# Revit family: LR1685-W-2
name_source: partatom
category: Plumbing Fixtures
revit_build: Autodesk Revit MEP 2016 (Build: 20150220_1215(x64)
units: mm (PartAtom-declared; Revit-internal decimal feet)

## family parameters
Cut with Voids When Loaded = No
Host = Face
OmniClass Number = 23.45.05.21.11.11
OmniClass Title = Water Operated Water Closets
Part Type = Normal
Room Calculation Point = No
Round Connector Dimension = Use Diameter
Shared = Yes

## types (1)
- LR1685-W-2
    2- On-Floor, Wall Outlet = Yes
    ADA - 18" Integral Seat Height = No
    CO1 - Cleanout w/ O-Ring Connection to No-Hub 4" (Plain End Only) = No
    CO1-3 - Cleanout w/ O-Ring Connection to No-Hub 3" (Plain End Only) = No
    COH - Cleanout Hook Assembly = No
    CW Connection = No
    Default Elevation = 15"
    Description = Ligature Resistant Blowout Jet Toilet Bowl -On Floor-
    EG - Enviro-Glaze Toilet Exterior & Interior Color Specify = No
    EGE -EG - Enviro-Glaze Toilet Exterior Only Color Specify = No
    EVSFV- Master-Trol Electronic Flush Valve (N/A for Top Supply) = No
    EVSPFV- Master-Trol Electronic Flush Valve w/ Piezo Button (N/A for Top Supply) = No
    FT - Flood-Trol (N/A With Top Supply) = No
    FTA - Flood-Trol Auto-Reset (N/A with Top Supply) = No
    FTE - Flood-Trol Electronic = No
    FV- Flush Valve, Mechanical (N/A for ADA) = 0"
    FVBO- Flush Valve by Others = No
    FVH- Flush Valve, Hydraulic (N/A for Top Supply) = No
    FVT - Flush Thru-Wall Connector = No
    GW - Gasketed Toilet Waste = No
    HET- 1.28 GPF = No
    HPS - High Polish Integral Seat = No
    HW Connection = No
    LR1685- Ligature Resistant Blowout Jet Toilet = Yes
    MT - Metal Template (Only 1 Repuired Per Project) = No
    MTPFV- Master-Trol Plus Electronic Flush Valve (N/A for Top Supply) = No
    MTPPFV- Master-Trol Plus Electronic Flush Valve W/ Piezo Button (N/A for Top Supply) = No
    MVCFV- Time-Trol Plus Electronic Flush Valve (N/A for Top Supply) = No
    Manufacturer = Acorn Engineering
    Material = Type 304 Stainless Steel
    Model = LR1685-W-2
    PC - Pinned Cleanout Plug (For -C01 Options Above) = No
    SW - Wall Sleeve = No
    T- Top (exposed) = No
    TF - Transformer 120VAC to 24 VAC (-MVCFV option) = No
    TG - 12 Gage Housing = No
    TSC - Toilet Shipping Cover = No
    TWE - Toilet Waste Extension (3" Standard) Specify Length Beyond Fixture = No
    ULF- 1.6 GPF (Not Available in California) = No
    URL = http://www.acorneng.com
    VAC - AcornVac System = No
    Vent Connection = No
    W- Wall (Concealed) = No
    WO3B - 3" Bell Waste Outlet W/ Std 2-3/8" Trap = No
    Waste Connection = Yes

## geometry (parser evidence)
native form markers: Sweep x2
no freeform markers — native parametric forms only
